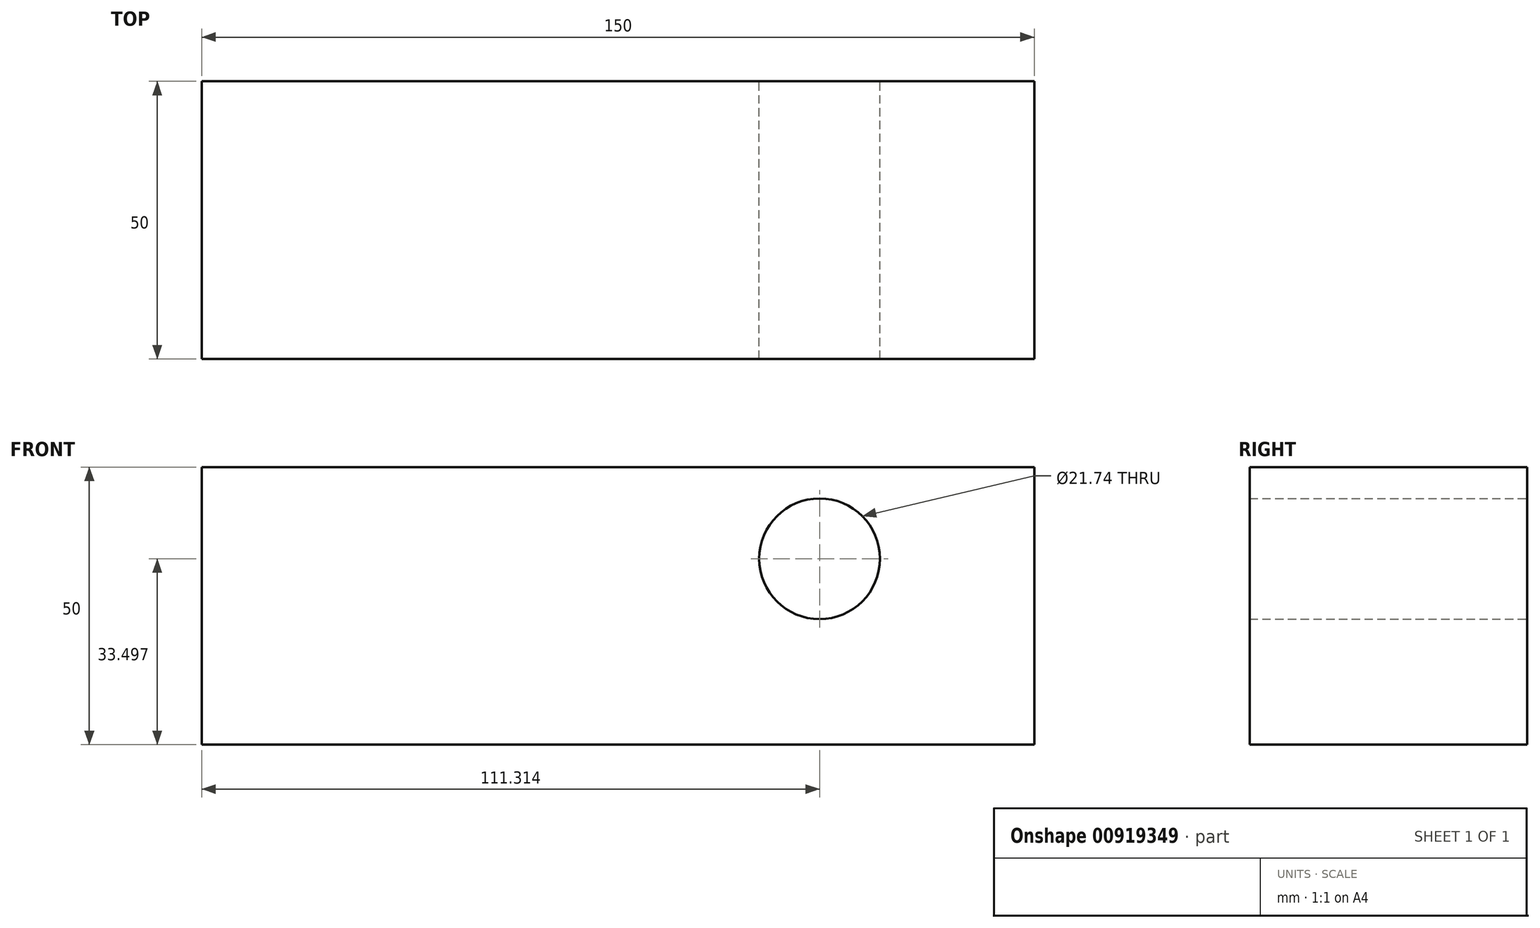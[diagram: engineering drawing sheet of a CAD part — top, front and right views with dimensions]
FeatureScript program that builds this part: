
annotation { "Feature Type Name" : "Feature", "Feature Type Description" : "" }
export const myFeature = defineFeature(function(context is Context, id is Id, definition is map)
    precondition{}
    {
        {
            var Q0;
            Q0=qCreatedBy(makeId("Front.planeOp"),FACE);
            var sketch = newSketch(context, id + "F0", { "sketchPlane" : qUnion([Q0])});
            skLineSegment(sketch, "E0.bottom", {"start": v(-70.93, 50) * mm, "end": v(79.07, 50) * mm});
            skLineSegment(sketch, "E0.top", {"start": v(-70.93, 0) * mm, "end": v(79.07, 0) * mm});
            skLineSegment(sketch, "E0.left", {"start": v(-70.93, 50) * mm, "end": v(-70.93, 0) * mm});
            skLineSegment(sketch, "E0.right", {"start": v(79.07, 50) * mm, "end": v(79.07, 0) * mm});
            skSolve(sketch);
        }
        {
            var Q0;
            Q0 = qSketchRegion(id + "F0", true);
            extrude(context, id + "F1", {"entities" : qUnion([Q0]), "depth" : 50 * mm, "offsetDistance" : 25 * mm});
        }
        {
            var Q0;
            Q0=makeQuery(id+"F1.opExtrude","CAP_FACE",FACE,{"disambiguationData":[OSD([sQuery(id+"F0.wireOp",EDGE,"E0.bottom"),sQuery(id+"F0.wireOp",EDGE,"E0.top"),sQuery(id+"F0.wireOp",EDGE,"E0.left"),sQuery(id+"F0.wireOp",EDGE,"E0.right")])],"isStart":false});
            var sketch = newSketch(context, id + "F2", { "sketchPlane" : qUnion([Q0])});
            skCircle(sketch, "E1", {"center": v(-41.18, 25.25) * mm, "radius": 9.75 * mm});
            skSolve(sketch);
        }
        {
            var Q0;
            Q0=sQuery(id+"F2.wireOp",EDGE,"E1");
            extrude(context, id + "F3", {"bodyType" : ToolBodyType.SURFACE, "surfaceEntities" : qUnion([Q0]), "endBound" : BoundingType.THROUGH_ALL, "depth" : 25 * mm, "offsetDistance" : 25 * mm});
        }
        {
            var Q0;
            Q0=makeQuery(id+"F1.opExtrude","CAP_FACE",FACE,{"disambiguationData":[OSD([sQuery(id+"F0.wireOp",EDGE,"E0.bottom"),sQuery(id+"F0.wireOp",EDGE,"E0.top"),sQuery(id+"F0.wireOp",EDGE,"E0.left"),sQuery(id+"F0.wireOp",EDGE,"E0.right")])],"isStart":true});
            var sketch = newSketch(context, id + "F4", { "sketchPlane" : qUnion([Q0])});
            skCircle(sketch, "E2", {"center": v(-40.38, 33.5) * mm, "radius": 10.87 * mm});
            skSolve(sketch);
        }
        {
            var Q0;
            Q0 = qSketchRegion(id + "F4", true);
            extrude(context, id + "F5", {"entities" : qUnion([Q0]), "operationType" : NewBodyOperationType.REMOVE, "oppositeDirection" : true, "depth" : 61 * mm, "offsetDistance" : 25 * mm});
        }
    });
